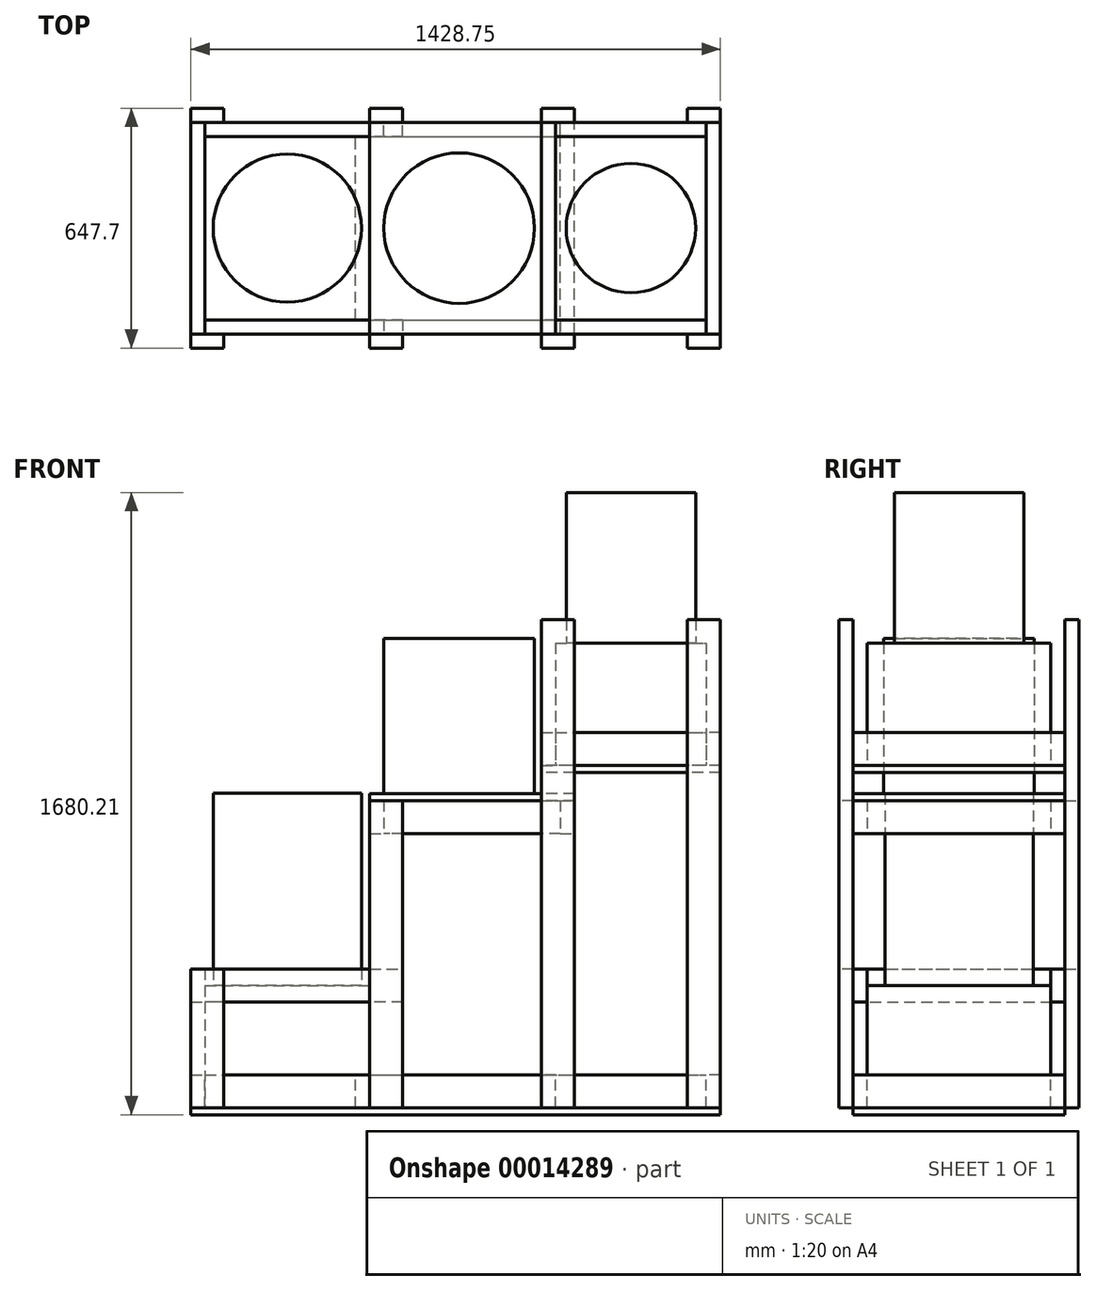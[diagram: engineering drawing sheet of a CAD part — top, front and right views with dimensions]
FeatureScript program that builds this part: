
annotation { "Feature Type Name" : "Feature", "Feature Type Description" : "" }
export const myFeature = defineFeature(function(context is Context, id is Id, definition is map)
    precondition{}
    {
        {
            var Q0;
            Q0=qCreatedBy(makeId("Top.planeOp"),FACE);
            var sketch = newSketch(context, id + "F0", { "sketchPlane" : qUnion([Q0])});
            skCircle(sketch, "E0", {"center": v(0, 0) * mm, "radius": 200.02 * mm});
            skCircle(sketch, "E1", {"center": v(463.55, 0) * mm, "radius": 203.2 * mm});
            skCircle(sketch, "E2", {"center": v(927.1, 0) * mm, "radius": 174.63 * mm});
            skLineSegment(sketch, "E3", {"start": v(-200.02, 0) * mm, "end": v(1101.73, 0) * mm, "construction": true});
            skLineSegment(sketch, "E4.rect.bottom", {"start": v(-260.35, 285.75) * mm, "end": v(260.35, 285.75) * mm});
            skLineSegment(sketch, "E4.rect.top", {"start": v(-260.35, -285.75) * mm, "end": v(260.35, -285.75) * mm});
            skLineSegment(sketch, "E4.rect.left", {"start": v(-260.35, 285.75) * mm, "end": v(-260.35, -285.75) * mm});
            skLineSegment(sketch, "E4.rect.right", {"start": v(260.35, 285.75) * mm, "end": v(260.35, -285.75) * mm});
            skLineSegment(sketch, "E5.rect.bottom", {"start": v(-222.25, 247.65) * mm, "end": v(222.25, 247.65) * mm});
            skLineSegment(sketch, "E5.rect.top", {"start": v(-222.25, -247.65) * mm, "end": v(222.25, -247.65) * mm});
            skLineSegment(sketch, "E5.rect.left", {"start": v(-222.25, 247.65) * mm, "end": v(-222.25, -247.65) * mm});
            skLineSegment(sketch, "E5.rect.right", {"start": v(222.25, 247.65) * mm, "end": v(222.25, -247.65) * mm});
            skLineSegment(sketch, "E6.rect.bottom", {"start": v(723.9, 247.65) * mm, "end": v(1130.3, 247.65) * mm});
            skLineSegment(sketch, "E6.rect.top", {"start": v(723.9, -247.65) * mm, "end": v(1130.3, -247.65) * mm});
            skLineSegment(sketch, "E6.rect.left", {"start": v(723.9, 247.65) * mm, "end": v(723.9, -247.65) * mm});
            skLineSegment(sketch, "E6.rect.right", {"start": v(1130.3, 247.65) * mm, "end": v(1130.3, -247.65) * mm});
            skLineSegment(sketch, "E7.rect.bottom", {"start": v(685.8, 285.75) * mm, "end": v(1168.4, 285.75) * mm});
            skLineSegment(sketch, "E7.rect.top", {"start": v(685.8, -285.75) * mm, "end": v(1168.4, -285.75) * mm});
            skLineSegment(sketch, "E7.rect.left", {"start": v(685.8, 285.75) * mm, "end": v(685.8, -285.75) * mm});
            skLineSegment(sketch, "E7.rect.right", {"start": v(1168.4, 285.75) * mm, "end": v(1168.4, -285.75) * mm});
            skSolve(sketch);
        }
        {
            var Q0;
            Q0=qCreatedBy(makeId("Front.planeOp"),FACE);
            var sketch = newSketch(context, id + "F1", { "sketchPlane" : qUnion([Q0])});
            skLineSegment(sketch, "E8", {"start": v(0, -177.8) * mm, "end": v(0, 19.05) * mm});
            skPoint(sketch, "E9.0", {"position": v(463.55, 0) * mm});
            skPoint(sketch, "E10.0", {"position": v(927.1, 0) * mm});
            skLineSegment(sketch, "E11", {"start": v(463.55, 829.31) * mm, "end": v(463.55, 1267.46) * mm});
            skLineSegment(sketch, "E12", {"start": v(927.1, 1292.86) * mm, "end": v(927.1, 1318.26) * mm});
            skLineSegment(sketch, "E13", {"start": v(0, 349.25) * mm, "end": v(0, 374.65) * mm});
            skLineSegment(sketch, "E14", {"start": v(927.1, 1292.86) * mm, "end": v(927.1, 962.66) * mm});
            skLineSegment(sketch, "E15", {"start": v(0, 19.05) * mm, "end": v(0, 349.25) * mm});
            skLineSegment(sketch, "E16", {"start": v(0, 374.65) * mm, "end": v(0, 829.3) * mm});
            skLineSegment(sketch, "E17", {"start": v(927.1, 1318.26) * mm, "end": v(927.1, 1711.96) * mm});
            skSolve(sketch);
        }
        {
            var Q0;
            Q0=sQuery(id+"F1.wireOp",VERTEX,"E13.end");
            var Q1;
            Q1=qCreatedBy(makeId("Top.planeOp"),FACE);
            cPlane(context, id + "F2", {"entities" : qUnion([Q0, Q1]), "cplaneType" : CPlaneType.PLANE_POINT, "offset" : 152.4 * mm, "width" : 152.4 * mm, "height" : 152.4 * mm});
        }
        {
            var Q0;
            Q0=sQuery(id+"F1.wireOp",VERTEX,"E11.start");
            var Q1;
            Q1=qCreatedBy(makeId("Top.planeOp"),FACE);
            cPlane(context, id + "F3", {"entities" : qUnion([Q0, Q1]), "cplaneType" : CPlaneType.PLANE_POINT, "offset" : 152.4 * mm, "width" : 152.4 * mm, "height" : 152.4 * mm});
        }
        {
            var Q0;
            Q0=sQuery(id+"F1.wireOp",VERTEX,"E12.end");
            var Q1;
            Q1=qCreatedBy(makeId("Top.planeOp"),FACE);
            cPlane(context, id + "F4", {"entities" : qUnion([Q0, Q1]), "cplaneType" : CPlaneType.PLANE_POINT, "offset" : 152.4 * mm, "width" : 152.4 * mm, "height" : 152.4 * mm});
        }
        {
            var Q0;
            Q0=qCreatedBy(makeId("Top.planeOp"),FACE);
            var sketch = newSketch(context, id + "F5", { "sketchPlane" : qUnion([Q0])});
            skPoint(sketch, "E18.0", {"position": v(-260.35, 285.75) * mm});
            skPoint(sketch, "E19.0", {"position": v(1168.4, 285.75) * mm});
            skPoint(sketch, "E20.0", {"position": v(-222.25, 247.65) * mm});
            skPoint(sketch, "E21.0", {"position": v(222.25, 247.65) * mm});
            skPoint(sketch, "E22.0", {"position": v(260.35, 285.75) * mm});
            skPoint(sketch, "E23.0", {"position": v(685.8, 285.75) * mm});
            skPoint(sketch, "E24.0", {"position": v(723.9, 247.65) * mm});
            skPoint(sketch, "E25.0", {"position": v(1130.3, 247.65) * mm});
            skLineSegment(sketch, "E26.bottom", {"start": v(-260.35, 285.75) * mm, "end": v(-171.45, 285.75) * mm});
            skLineSegment(sketch, "E26.top", {"start": v(-260.35, 323.85) * mm, "end": v(-171.45, 323.85) * mm});
            skLineSegment(sketch, "E26.left", {"start": v(-260.35, 285.75) * mm, "end": v(-260.35, 323.85) * mm});
            skLineSegment(sketch, "E26.right", {"start": v(-171.45, 285.75) * mm, "end": v(-171.45, 323.85) * mm});
            skLineSegment(sketch, "E27.bottom", {"start": v(222.25, 285.75) * mm, "end": v(311.15, 285.75) * mm});
            skLineSegment(sketch, "E27.top", {"start": v(222.25, 323.85) * mm, "end": v(311.15, 323.85) * mm});
            skLineSegment(sketch, "E27.left", {"start": v(222.25, 285.75) * mm, "end": v(222.25, 323.85) * mm});
            skLineSegment(sketch, "E27.right", {"start": v(311.15, 285.75) * mm, "end": v(311.15, 323.85) * mm});
            skLineSegment(sketch, "E28.bottom", {"start": v(685.8, 285.75) * mm, "end": v(774.7, 285.75) * mm});
            skLineSegment(sketch, "E28.top", {"start": v(685.8, 323.85) * mm, "end": v(774.7, 323.85) * mm});
            skLineSegment(sketch, "E28.left", {"start": v(685.8, 285.75) * mm, "end": v(685.8, 323.85) * mm});
            skLineSegment(sketch, "E28.right", {"start": v(774.7, 285.75) * mm, "end": v(774.7, 323.85) * mm});
            skLineSegment(sketch, "E29.bottom", {"start": v(1079.5, 285.75) * mm, "end": v(1168.4, 285.75) * mm});
            skLineSegment(sketch, "E29.top", {"start": v(1079.5, 323.85) * mm, "end": v(1168.4, 323.85) * mm});
            skLineSegment(sketch, "E29.left", {"start": v(1079.5, 285.75) * mm, "end": v(1079.5, 323.85) * mm});
            skLineSegment(sketch, "E29.right", {"start": v(1168.4, 285.75) * mm, "end": v(1168.4, 323.85) * mm});
            skSolve(sketch);
        }
        {
            var Q0;
            Q0=makeQuery(id+"F5.imprint","IMPRINT",FACE,{"disambiguationData":[TD([[makeQuery(id+"F5.imprint","IMPRINT",EDGE,{"derivedFrom":sQuery(id+"F5.wireOp",EDGE,"E26.bottom")}),1.0]])]});
            var Q1;
            Q1=qCreatedBy(id+"F2.planeOp",FACE);
            extrude(context, id + "F6", {"entities" : qUnion([Q0]), "endBound" : BoundingType.UP_TO_SURFACE, "endBoundEntityFace" : qUnion([Q1]), "depth" : 330.2 * mm});
        }
        {
            var Q0;
            Q0=makeQuery(id+"F5.imprint","IMPRINT",FACE,{"disambiguationData":[TD([[makeQuery(id+"F5.imprint","IMPRINT",EDGE,{"derivedFrom":sQuery(id+"F5.wireOp",EDGE,"E27.bottom")}),1.0]])]});
            var Q1;
            Q1=qCreatedBy(id+"F3.planeOp",FACE);
            extrude(context, id + "F7", {"entities" : qUnion([Q0]), "endBound" : BoundingType.UP_TO_SURFACE, "endBoundEntityFace" : qUnion([Q1]), "depth" : 25.4 * mm});
        }
        {
            var Q0;
            Q0=makeQuery(id+"F5.imprint","IMPRINT",FACE,{"disambiguationData":[TD([[makeQuery(id+"F5.imprint","IMPRINT",EDGE,{"derivedFrom":sQuery(id+"F5.wireOp",EDGE,"E28.bottom")}),1.0]])]});
            var Q1;
            Q1=makeQuery(id+"F5.imprint","IMPRINT",FACE,{"disambiguationData":[TD([[makeQuery(id+"F5.imprint","IMPRINT",EDGE,{"derivedFrom":sQuery(id+"F5.wireOp",EDGE,"E29.bottom")}),1.0]])]});
            var Q2;
            Q2=qCreatedBy(id+"F4.planeOp",FACE);
            extrude(context, id + "F8", {"entities" : qUnion([Q0, Q1]), "endBound" : BoundingType.UP_TO_SURFACE, "endBoundEntityFace" : qUnion([Q2]), "depth" : 25.4 * mm});
        }
        {
            var Q0;
            Q0=makeQuery(id+"F6.opExtrude","SWEPT_FACE",FACE,{"disambiguationData":[OSD([sQuery(id+"F5.wireOp",EDGE,"E26.bottom")])]});
            var sketch = newSketch(context, id + "F9", { "sketchPlane" : qUnion([Q0])});
            skLineSegment(sketch, "E30.bottom", {"start": v(-260.35, 0) * mm, "end": v(-222.25, 0) * mm});
            skLineSegment(sketch, "E30.top", {"start": v(-260.35, 88.9) * mm, "end": v(-222.25, 88.9) * mm});
            skLineSegment(sketch, "E30.left", {"start": v(-260.35, 0) * mm, "end": v(-260.35, 88.9) * mm});
            skLineSegment(sketch, "E30.right", {"start": v(-222.25, 0) * mm, "end": v(-222.25, 88.9) * mm});
            skLineSegment(sketch, "E31.bottom", {"start": v(1168.4, 0) * mm, "end": v(1130.3, 0) * mm});
            skLineSegment(sketch, "E31.top", {"start": v(1168.4, 88.9) * mm, "end": v(1130.3, 88.9) * mm});
            skLineSegment(sketch, "E31.left", {"start": v(1168.4, 0) * mm, "end": v(1168.4, 88.9) * mm});
            skLineSegment(sketch, "E31.right", {"start": v(1130.3, 0) * mm, "end": v(1130.3, 88.9) * mm});
            skLineSegment(sketch, "E32.bottom", {"start": v(222.25, 829.31) * mm, "end": v(260.35, 829.31) * mm});
            skLineSegment(sketch, "E32.top", {"start": v(222.25, 740.41) * mm, "end": v(260.35, 740.41) * mm});
            skLineSegment(sketch, "E32.left", {"start": v(222.25, 829.31) * mm, "end": v(222.25, 740.41) * mm});
            skLineSegment(sketch, "E32.right", {"start": v(260.35, 829.31) * mm, "end": v(260.35, 740.41) * mm});
            skLineSegment(sketch, "E33.bottom", {"start": v(736.6, 829.31) * mm, "end": v(774.7, 829.31) * mm});
            skLineSegment(sketch, "E33.top", {"start": v(736.6, 740.41) * mm, "end": v(774.7, 740.41) * mm});
            skLineSegment(sketch, "E33.left", {"start": v(736.6, 829.3) * mm, "end": v(736.6, 740.41) * mm});
            skLineSegment(sketch, "E33.right", {"start": v(774.7, 829.31) * mm, "end": v(774.7, 740.41) * mm});
            skLineSegment(sketch, "E34.bottom", {"start": v(1168.4, 1013.46) * mm, "end": v(1130.3, 1013.46) * mm});
            skLineSegment(sketch, "E34.top", {"start": v(1168.4, 924.56) * mm, "end": v(1130.3, 924.56) * mm});
            skLineSegment(sketch, "E34.left", {"start": v(1168.4, 1013.46) * mm, "end": v(1168.4, 924.56) * mm});
            skLineSegment(sketch, "E34.right", {"start": v(1130.3, 1013.46) * mm, "end": v(1130.3, 924.56) * mm});
            skLineSegment(sketch, "E35.bottom", {"start": v(685.8, 1013.46) * mm, "end": v(723.9, 1013.46) * mm});
            skLineSegment(sketch, "E35.top", {"start": v(685.8, 924.56) * mm, "end": v(723.9, 924.56) * mm});
            skLineSegment(sketch, "E35.left", {"start": v(685.8, 1013.46) * mm, "end": v(685.8, 924.56) * mm});
            skLineSegment(sketch, "E35.right", {"start": v(723.9, 1013.46) * mm, "end": v(723.9, 924.56) * mm});
            skLineSegment(sketch, "E36", {"start": v(723.9, 1013.46) * mm, "end": v(1130.3, 1013.46) * mm});
            skLineSegment(sketch, "E37", {"start": v(1130.3, 924.56) * mm, "end": v(723.9, 924.56) * mm});
            skLineSegment(sketch, "E38", {"start": v(260.35, 829.31) * mm, "end": v(736.6, 829.31) * mm});
            skLineSegment(sketch, "E39", {"start": v(736.6, 740.41) * mm, "end": v(260.35, 740.41) * mm});
            skLineSegment(sketch, "E40", {"start": v(-222.25, 88.9) * mm, "end": v(1130.3, 88.9) * mm});
            skLineSegment(sketch, "E41", {"start": v(1130.3, 0) * mm, "end": v(-222.25, 0) * mm});
            skLineSegment(sketch, "E42.bottom", {"start": v(-260.35, 374.65) * mm, "end": v(-222.25, 374.65) * mm});
            skLineSegment(sketch, "E42.top", {"start": v(-260.35, 285.75) * mm, "end": v(-222.25, 285.75) * mm});
            skLineSegment(sketch, "E42.left", {"start": v(-260.35, 374.65) * mm, "end": v(-260.35, 285.75) * mm});
            skLineSegment(sketch, "E42.right", {"start": v(-222.25, 374.65) * mm, "end": v(-222.25, 285.75) * mm});
            skLineSegment(sketch, "E43", {"start": v(-222.25, 374.65) * mm, "end": v(311.15, 374.65) * mm});
            skLineSegment(sketch, "E44", {"start": v(311.15, 374.65) * mm, "end": v(311.15, 285.75) * mm});
            skLineSegment(sketch, "E45", {"start": v(311.15, 285.75) * mm, "end": v(-222.25, 285.75) * mm});
            skSolve(sketch);
        }
        {
            var Q0;
            {var subQ5=sQuery(id+"F9.wireOp",EDGE,"E30.right");Q0=makeQuery(id+"F9.imprint","IMPRINT",FACE,{"disambiguationData":[TD([[makeQuery(id+"F9.imprint","IMPRINT",EDGE,{"derivedFrom":subQ5}),-1.0]])]});}
            var Q1;
            {var subQ5=sQuery(id+"F9.wireOp",EDGE,"E31.right");Q1=makeQuery(id+"F9.imprint","IMPRINT",FACE,{"disambiguationData":[TD([[makeQuery(id+"F9.imprint","IMPRINT",EDGE,{"derivedFrom":subQ5}),1.0]])]});}
            var Q2;
            Q2=makeQuery(id+"F9.imprint","IMPRINT",FACE,{"disambiguationData":[TD([[makeQuery(id+"F9.imprint","IMPRINT",EDGE,{"derivedFrom":sQuery(id+"F9.wireOp",EDGE,"E32.right")}),1.0]])]});
            var Q3;
            Q3=makeQuery(id+"F9.imprint","IMPRINT",FACE,{"disambiguationData":[TD([[makeQuery(id+"F9.imprint","IMPRINT",EDGE,{"derivedFrom":sQuery(id+"F9.wireOp",EDGE,"E34.right")}),-1.0]])]});
            var Q4;
            {var subQ5=sQuery(id+"F9.wireOp",EDGE,"E42.right");Q4=makeQuery(id+"F9.imprint","IMPRINT",FACE,{"disambiguationData":[TD([[makeQuery(id+"F9.imprint","IMPRINT",EDGE,{"derivedFrom":subQ5}),1.0]])]});}
            var Q5;
            {var subQ5=sQuery(id+"F9.wireOp",EDGE,"E44");Q5=makeQuery(id+"F9.imprint","IMPRINT",FACE,{"disambiguationData":[TD([[makeQuery(id+"F9.imprint","IMPRINT",EDGE,{"derivedFrom":subQ5}),-1.0]])]});}
            extrude(context, id + "F10", {"entities" : qUnion([Q0, Q1, Q2, Q3, Q4, Q5]), "depth" : 38.1 * mm});
        }
        {
            var Q0;
            Q0=makeQuery(id+"F6.opExtrude","SWEPT_BODY",BODY,{"disambiguationData":[OSD([sQuery(id+"F5.wireOp",EDGE,"E26.bottom"),sQuery(id+"F5.wireOp",EDGE,"E26.top"),sQuery(id+"F5.wireOp",EDGE,"E26.left"),sQuery(id+"F5.wireOp",EDGE,"E26.right")])]});
            var Q1;
            Q1=makeQuery(id+"F7.opExtrude","SWEPT_BODY",BODY,{"disambiguationData":[OSD([sQuery(id+"F5.wireOp",EDGE,"E27.bottom"),sQuery(id+"F5.wireOp",EDGE,"E27.top"),sQuery(id+"F5.wireOp",EDGE,"E27.left"),sQuery(id+"F5.wireOp",EDGE,"E27.right")])]});
            var Q2;
            Q2=makeQuery(id+"F8.opExtrude","SWEPT_BODY",BODY,{"disambiguationData":[OSD([sQuery(id+"F5.wireOp",EDGE,"E28.bottom"),sQuery(id+"F5.wireOp",EDGE,"E28.top"),sQuery(id+"F5.wireOp",EDGE,"E28.left"),sQuery(id+"F5.wireOp",EDGE,"E28.right")])]});
            var Q3;
            Q3=makeQuery(id+"F8.opExtrude","SWEPT_BODY",BODY,{"disambiguationData":[OSD([sQuery(id+"F5.wireOp",EDGE,"E29.bottom"),sQuery(id+"F5.wireOp",EDGE,"E29.top"),sQuery(id+"F5.wireOp",EDGE,"E29.left"),sQuery(id+"F5.wireOp",EDGE,"E29.right")])]});
            var Q4;
            Q4=makeQuery(id+"F10.opExtrude","SWEPT_BODY",BODY,{"disambiguationData":[OSD([sQuery(id+"F9.wireOp",EDGE,"E34.right"),sQuery(id+"F9.wireOp",EDGE,"E35.right"),sQuery(id+"F9.wireOp",EDGE,"E36"),sQuery(id+"F9.wireOp",EDGE,"E37")])]});
            var Q5;
            Q5=makeQuery(id+"F10.opExtrude","SWEPT_BODY",BODY,{"disambiguationData":[OSD([sQuery(id+"F9.wireOp",EDGE,"E32.right"),sQuery(id+"F9.wireOp",EDGE,"E33.left"),sQuery(id+"F9.wireOp",EDGE,"E38"),sQuery(id+"F9.wireOp",EDGE,"E39")])]});
            var Q6;
            Q6=makeQuery(id+"F10.opExtrude","SWEPT_BODY",BODY,{"disambiguationData":[OSD([sQuery(id+"F9.wireOp",EDGE,"E30.right"),sQuery(id+"F9.wireOp",EDGE,"E31.right"),sQuery(id+"F9.wireOp",EDGE,"E40"),sQuery(id+"F9.wireOp",EDGE,"E41")])]});
            var Q7;
            Q7=makeQuery(id+"F10.opExtrude","SWEPT_BODY",BODY,{"disambiguationData":[OSD([sQuery(id+"F9.wireOp",EDGE,"E42.right"),sQuery(id+"F9.wireOp",EDGE,"E43"),sQuery(id+"F9.wireOp",EDGE,"E44"),sQuery(id+"F9.wireOp",EDGE,"E45")])]});
            var Q8;
            Q8=qCreatedBy(makeId("Front.planeOp"),FACE);
            mirror(context, id + "F11", {"entities" : qUnion([Q0, Q1, Q2, Q3, Q4, Q5, Q6, Q7]), "mirrorPlane" : qUnion([Q8])});
        }
        {
            var Q0;
            Q0=makeQuery(id+"F9.imprint","IMPRINT",FACE,{"disambiguationData":[TD([[makeQuery(id+"F9.imprint","IMPRINT",EDGE,{"derivedFrom":sQuery(id+"F9.wireOp",EDGE,"E30.bottom")}),1.0]])]});
            var Q1;
            Q1=makeQuery(id+"F9.imprint","IMPRINT",FACE,{"disambiguationData":[TD([[makeQuery(id+"F9.imprint","IMPRINT",EDGE,{"derivedFrom":sQuery(id+"F9.wireOp",EDGE,"E32.bottom")}),-1.0]])]});
            var Q2;
            Q2=makeQuery(id+"F9.imprint","IMPRINT",FACE,{"disambiguationData":[TD([[makeQuery(id+"F9.imprint","IMPRINT",EDGE,{"derivedFrom":sQuery(id+"F9.wireOp",EDGE,"E33.bottom")}),-1.0]])]});
            var Q3;
            Q3=makeQuery(id+"F9.imprint","IMPRINT",FACE,{"disambiguationData":[TD([[makeQuery(id+"F9.imprint","IMPRINT",EDGE,{"derivedFrom":sQuery(id+"F9.wireOp",EDGE,"E35.bottom")}),-1.0]])]});
            var Q4;
            Q4=makeQuery(id+"F9.imprint","IMPRINT",FACE,{"disambiguationData":[TD([[makeQuery(id+"F9.imprint","IMPRINT",EDGE,{"derivedFrom":sQuery(id+"F9.wireOp",EDGE,"E31.bottom")}),-1.0]])]});
            var Q5;
            Q5=makeQuery(id+"F9.imprint","IMPRINT",FACE,{"disambiguationData":[TD([[makeQuery(id+"F9.imprint","IMPRINT",EDGE,{"derivedFrom":sQuery(id+"F9.wireOp",EDGE,"E34.bottom")}),1.0]])]});
            var Q6;
            Q6=makeQuery(id+"F9.imprint","IMPRINT",FACE,{"disambiguationData":[TD([[makeQuery(id+"F9.imprint","IMPRINT",EDGE,{"derivedFrom":sQuery(id+"F9.wireOp",EDGE,"E42.bottom")}),-1.0]])]});
            var Q7;
            Q7=makeQuery(id+"F11.opPattern","COPY",FACE,{"derivedFrom":makeQuery(id+"F8.opExtrude","SWEPT_FACE",FACE,{"disambiguationData":[OSD([sQuery(id+"F5.wireOp",EDGE,"E29.bottom")])]}),"instanceName":"1"});
            extrude(context, id + "F12", {"entities" : qUnion([Q0, Q1, Q2, Q3, Q4, Q5, Q6]), "endBound" : BoundingType.UP_TO_SURFACE, "endBoundEntityFace" : qUnion([Q7]), "depth" : 25.4 * mm});
        }
        {
            var Q0;
            Q0=makeQuery(id+"F12.opExtrude","SWEPT_FACE",FACE,{"disambiguationData":[OSD([sQuery(id+"F9.wireOp",EDGE,"E32.bottom")])]});
            var sketch = newSketch(context, id + "F13", { "sketchPlane" : qUnion([Q0])});
            skLineSegment(sketch, "E46.bottom", {"start": v(774.7, 285.75) * mm, "end": v(222.25, 285.75) * mm});
            skLineSegment(sketch, "E46.top", {"start": v(774.7, -285.75) * mm, "end": v(222.25, -285.75) * mm});
            skLineSegment(sketch, "E46.left", {"start": v(774.7, 285.75) * mm, "end": v(774.7, -285.75) * mm});
            skLineSegment(sketch, "E46.right", {"start": v(222.25, 285.75) * mm, "end": v(222.25, -285.75) * mm});
            skSolve(sketch);
        }
        {
            var Q0;
            Q0 = qSketchRegion(id + "F13", true);
            extrude(context, id + "F14", {"entities" : qUnion([Q0]), "depth" : 19.05 * mm});
        }
        {
            var Q0;
            Q0=qCreatedBy(makeId("Top.planeOp"),FACE);
            var sketch = newSketch(context, id + "F15", { "sketchPlane" : qUnion([Q0])});
            skLineSegment(sketch, "E47.bottom", {"start": v(-260.35, -285.75) * mm, "end": v(1168.4, -285.75) * mm});
            skLineSegment(sketch, "E47.top", {"start": v(-260.35, 285.75) * mm, "end": v(1168.4, 285.75) * mm});
            skLineSegment(sketch, "E47.left", {"start": v(-260.35, -285.75) * mm, "end": v(-260.35, 285.75) * mm});
            skLineSegment(sketch, "E47.right", {"start": v(1168.4, -285.75) * mm, "end": v(1168.4, 285.75) * mm});
            skSolve(sketch);
        }
        {
            var Q0;
            Q0 = qSketchRegion(id + "F15", true);
            extrude(context, id + "F16", {"entities" : qUnion([Q0]), "oppositeDirection" : true, "depth" : 19.05 * mm});
        }
        {
            var Q0;
            Q0=makeQuery(id+"F0.imprint","IMPRINT",FACE,{"disambiguationData":[TD([[makeQuery(id+"F0.imprint","IMPRINT",EDGE,{"derivedFrom":sQuery(id+"F0.wireOp",EDGE,"E0")}),-1.0]])]});
            var Q1;
            Q1=makeQuery(id+"F0.imprint","IMPRINT",FACE,{"disambiguationData":[TD([[makeQuery(id+"F0.imprint","IMPRINT",EDGE,{"derivedFrom":sQuery(id+"F0.wireOp",EDGE,"E0")}),1.0]])]});
            extrude(context, id + "F17", {"entities" : qUnion([Q0, Q1]), "depth" : 330.2 * mm});
        }
        {
            var Q0;
            Q0=makeQuery(id+"F17.opExtrude","CAP_FACE",FACE,{"disambiguationData":[OSD([sQuery(id+"F0.wireOp",EDGE,"E5.rect.bottom"),sQuery(id+"F0.wireOp",EDGE,"E5.rect.top"),sQuery(id+"F0.wireOp",EDGE,"E5.rect.left"),sQuery(id+"F0.wireOp",EDGE,"E5.rect.right")])],"isStart":false});
            var sketch = newSketch(context, id + "F18", { "sketchPlane" : qUnion([Q0])});
            skCircle(sketch, "E48.0", {"center": v(0, 0) * mm, "radius": 200.02 * mm});
            skSolve(sketch);
        }
        {
            var Q0;
            Q0=makeQuery(id+"F18.imprint","IMPRINT",FACE,{"disambiguationData":[TD([[makeQuery(id+"F18.imprint","IMPRINT",EDGE,{"derivedFrom":sQuery(id+"F18.wireOp",EDGE,"E48.0")}),1.0]])]});
            extrude(context, id + "F19", {"entities" : qUnion([Q0]), "depth" : 518.34 * mm});
        }
        {
            var Q0;
            Q0=makeQuery(id+"F14.opExtrude","CAP_FACE",FACE,{"disambiguationData":[OSD([sQuery(id+"F13.wireOp",EDGE,"E46.bottom"),sQuery(id+"F13.wireOp",EDGE,"E46.top"),sQuery(id+"F13.wireOp",EDGE,"E46.left"),sQuery(id+"F13.wireOp",EDGE,"E46.right")])],"isStart":false});
            var sketch = newSketch(context, id + "F20", { "sketchPlane" : qUnion([Q0])});
            skCircle(sketch, "E49.0", {"center": v(463.55, 0) * mm, "radius": 203.2 * mm});
            skSolve(sketch);
        }
        {
            var Q0;
            Q0 = qSketchRegion(id + "F20", true);
            extrude(context, id + "F21", {"entities" : qUnion([Q0]), "depth" : 418.43 * mm});
        }
        {
            var Q0;
            Q0=makeQuery(id+"F12.opExtrude","SWEPT_FACE",FACE,{"disambiguationData":[OSD([sQuery(id+"F9.wireOp",EDGE,"E34.top")])]});
            var sketch = newSketch(context, id + "F22", { "sketchPlane" : qUnion([Q0])});
            skLineSegment(sketch, "E50.bottom", {"start": v(1168.4, 285.75) * mm, "end": v(685.8, 285.75) * mm});
            skLineSegment(sketch, "E50.top", {"start": v(1168.4, -285.75) * mm, "end": v(685.8, -285.75) * mm});
            skLineSegment(sketch, "E50.left", {"start": v(1168.4, 285.75) * mm, "end": v(1168.4, -285.75) * mm});
            skLineSegment(sketch, "E50.right", {"start": v(685.8, 285.75) * mm, "end": v(685.8, -285.75) * mm});
            skSolve(sketch);
        }
        {
            var Q0;
            {var subQ1=sQuery(id+"F22.wireOp",EDGE,"E50.right");Q0=makeQuery(id+"F22.imprint","IMPRINT",FACE,{"disambiguationData":[TD([[makeQuery(id+"F22.imprint","IMPRINT",EDGE,{"derivedFrom":subQ1}),1.0]])]});}
            var Q1;
            {var subQ1=sQuery(id+"F22.wireOp",EDGE,"E50.left");Q1=makeQuery(id+"F22.imprint","IMPRINT",FACE,{"disambiguationData":[TD([[makeQuery(id+"F22.imprint","IMPRINT",EDGE,{"derivedFrom":subQ1}),-1.0]])]});}
            extrude(context, id + "F23", {"entities" : qUnion([Q0, Q1]), "depth" : 19.05 * mm});
        }
        {
            var Q0;
            Q0=makeQuery(id+"F23.opExtrude","CAP_FACE",FACE,{"disambiguationData":[OSD([sQuery(id+"F22.wireOp",EDGE,"E50.bottom"),sQuery(id+"F22.wireOp",EDGE,"E50.top"),sQuery(id+"F22.wireOp",EDGE,"E50.left"),sQuery(id+"F22.wireOp",EDGE,"E50.right")])],"isStart":true});
            var sketch = newSketch(context, id + "F24", { "sketchPlane" : qUnion([Q0])});
            skLineSegment(sketch, "E51.0", {"start": v(723.9, 247.65) * mm, "end": v(1130.3, 247.65) * mm});
            skLineSegment(sketch, "E52.0", {"start": v(723.9, 247.65) * mm, "end": v(723.9, -247.65) * mm});
            skLineSegment(sketch, "E53.0", {"start": v(723.9, -247.65) * mm, "end": v(1130.3, -247.65) * mm});
            skLineSegment(sketch, "E54.0", {"start": v(1130.3, 247.65) * mm, "end": v(1130.3, -247.65) * mm});
            skSolve(sketch);
        }
        {
            var Q0;
            Q0 = qSketchRegion(id + "F24", true);
            extrude(context, id + "F25", {"entities" : qUnion([Q0]), "depth" : 330.2 * mm});
        }
        {
            var Q0;
            Q0=makeQuery(id+"F25.opExtrude","CAP_FACE",FACE,{"disambiguationData":[OSD([sQuery(id+"F24.wireOp",EDGE,"E51.0"),sQuery(id+"F24.wireOp",EDGE,"E52.0"),sQuery(id+"F24.wireOp",EDGE,"E53.0"),sQuery(id+"F24.wireOp",EDGE,"E54.0")])],"isStart":false});
            var sketch = newSketch(context, id + "F26", { "sketchPlane" : qUnion([Q0])});
            skCircle(sketch, "E55.0", {"center": v(927.1, 0) * mm, "radius": 174.63 * mm});
            skSolve(sketch);
        }
        {
            var Q0;
            Q0 = qSketchRegion(id + "F26", true);
            extrude(context, id + "F27", {"entities" : qUnion([Q0]), "depth" : 406.4 * mm});
        }
        {
            var Q0;
            Q0=makeQuery(id+"F10.opExtrude","CAP_FACE",FACE,{"disambiguationData":[OSD([sQuery(id+"F9.wireOp",EDGE,"E30.right"),sQuery(id+"F9.wireOp",EDGE,"E31.right"),sQuery(id+"F9.wireOp",EDGE,"E40"),sQuery(id+"F9.wireOp",EDGE,"E41")])],"isStart":false});
            var sketch = newSketch(context, id + "F28", { "sketchPlane" : qUnion([Q0])});
            skLineSegment(sketch, "E56.bottom", {"start": v(184.15, 88.9) * mm, "end": v(222.25, 88.9) * mm});
            skLineSegment(sketch, "E56.top", {"start": v(184.15, 0) * mm, "end": v(222.25, 0) * mm});
            skLineSegment(sketch, "E56.left", {"start": v(184.15, 88.9) * mm, "end": v(184.15, 0) * mm});
            skLineSegment(sketch, "E56.right", {"start": v(222.25, 88.9) * mm, "end": v(222.25, 0) * mm});
            skLineSegment(sketch, "E57.bottom", {"start": v(685.8, 88.9) * mm, "end": v(723.9, 88.9) * mm});
            skLineSegment(sketch, "E57.top", {"start": v(685.8, 0) * mm, "end": v(723.9, 0) * mm});
            skLineSegment(sketch, "E57.left", {"start": v(685.8, 88.9) * mm, "end": v(685.8, 0) * mm});
            skLineSegment(sketch, "E57.right", {"start": v(723.9, 88.9) * mm, "end": v(723.9, 0) * mm});
            skSolve(sketch);
        }
        {
            var Q0;
            Q0=makeQuery(id+"F28.imprint","IMPRINT",FACE,{"disambiguationData":[TD([[makeQuery(id+"F28.imprint","IMPRINT",EDGE,{"derivedFrom":sQuery(id+"F28.wireOp",EDGE,"E56.bottom")}),-1.0]])]});
            var Q1;
            Q1=makeQuery(id+"F28.imprint","IMPRINT",FACE,{"disambiguationData":[TD([[makeQuery(id+"F28.imprint","IMPRINT",EDGE,{"derivedFrom":sQuery(id+"F28.wireOp",EDGE,"E57.bottom")}),-1.0]])]});
            var Q2;
            Q2=makeQuery(id+"F11.opPattern","COPY",FACE,{"derivedFrom":makeQuery(id+"F10.opExtrude","CAP_FACE",FACE,{"disambiguationData":[OSD([sQuery(id+"F9.wireOp",EDGE,"E30.right"),sQuery(id+"F9.wireOp",EDGE,"E31.right"),sQuery(id+"F9.wireOp",EDGE,"E40"),sQuery(id+"F9.wireOp",EDGE,"E41")])],"isStart":false}),"instanceName":"1"});
            extrude(context, id + "F29", {"entities" : qUnion([Q0, Q1]), "endBound" : BoundingType.UP_TO_SURFACE, "endBoundEntityFace" : qUnion([Q2]), "depth" : 25.4 * mm});
        }
    });
